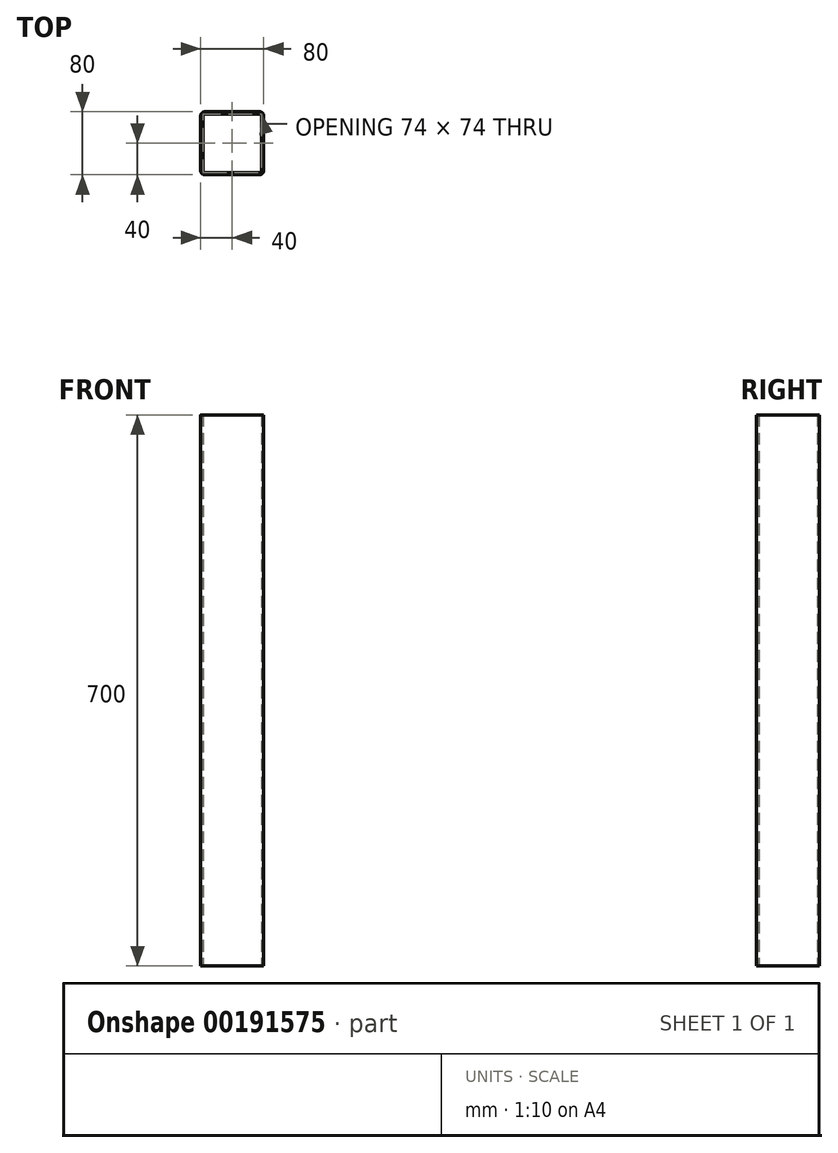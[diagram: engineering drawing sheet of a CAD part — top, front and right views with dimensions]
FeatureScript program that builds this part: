
annotation { "Feature Type Name" : "Feature", "Feature Type Description" : "" }
export const myFeature = defineFeature(function(context is Context, id is Id, definition is map)
    precondition{}
    {
        {
            var Q0;
            Q0=qCreatedBy(makeId("Top.planeOp"),FACE);
            var sketch = newSketch(context, id + "F0", { "sketchPlane" : qUnion([Q0])});
            skLineSegment(sketch, "E0.bottom", {"start": v(35, 40) * mm, "end": v(-35, 40) * mm});
            skLineSegment(sketch, "E0.top", {"start": v(35, -40) * mm, "end": v(-35, -40) * mm});
            skLineSegment(sketch, "E0.left", {"start": v(40, 35) * mm, "end": v(40, -35) * mm});
            skLineSegment(sketch, "E0.right", {"start": v(-40, 35) * mm, "end": v(-40, -35) * mm});
            skPoint(sketch, "E0.middle", {"position": v(0, 0) * mm});
            skPoint(sketch, "E1.visualSharp", {"position": v(-40, 40) * mm});
            skArc(sketch, "E1.filletArc", {"start": v(-35, 40) * mm, "mid": v(-38.54, 38.54) * mm, "end": v(-40, 35) * mm});
            skPoint(sketch, "E2.visualSharp", {"position": v(40, 40) * mm});
            skArc(sketch, "E2.filletArc", {"start": v(40, 35) * mm, "mid": v(38.54, 38.54) * mm, "end": v(35, 40) * mm});
            skPoint(sketch, "E3.visualSharp", {"position": v(40, -40) * mm});
            skArc(sketch, "E3.filletArc", {"start": v(35, -40) * mm, "mid": v(38.54, -38.54) * mm, "end": v(40, -35) * mm});
            skPoint(sketch, "E4.visualSharp", {"position": v(-40, -40) * mm});
            skArc(sketch, "E4.filletArc", {"start": v(-40, -35) * mm, "mid": v(-38.54, -38.54) * mm, "end": v(-35, -40) * mm});
            skLineSegment(sketch, "E5.0", {"start": v(-37, 35) * mm, "end": v(-37, -35) * mm});
            skArc(sketch, "E6.0", {"start": v(-35, 37) * mm, "mid": v(-36.41, 36.41) * mm, "end": v(-37, 35) * mm});
            skLineSegment(sketch, "E6.1", {"start": v(35, 37) * mm, "end": v(-35, 37) * mm});
            skArc(sketch, "E6.2", {"start": v(37, 35) * mm, "mid": v(36.41, 36.41) * mm, "end": v(35, 37) * mm});
            skArc(sketch, "E6.3", {"start": v(-37, -35) * mm, "mid": v(-36.41, -36.41) * mm, "end": v(-35, -37) * mm});
            skLineSegment(sketch, "E6.4", {"start": v(35, -37) * mm, "end": v(-35, -37) * mm});
            skArc(sketch, "E6.5", {"start": v(35, -37) * mm, "mid": v(36.41, -36.41) * mm, "end": v(37, -35) * mm});
            skLineSegment(sketch, "E6.6", {"start": v(37, 35) * mm, "end": v(37, -35) * mm});
            skSolve(sketch);
        }
        {
            var Q0;
            Q0 = qSketchRegion(id + "F0", true);
            extrude(context, id + "F1", {"entities" : qUnion([Q0]), "depth" : 700 * mm});
        }
    });
